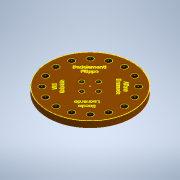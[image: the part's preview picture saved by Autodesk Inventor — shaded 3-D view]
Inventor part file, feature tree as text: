
AUTODESK INVENTOR PART (.ipt)
format: ipt  version: 2020.2 (Build 242310000, 310)  size: 1,744,896 bytes
history: native  units: mm
features: sketch x5, extrude x2, hole x2, other x1
ambient origin geometry x8: Origin, YZ Plane, XZ Plane, XY Plane, X Axis, Y Axis, Z Axis, Center Point
bodies: Solido1 (feature_tree)
feature tree (10):
  extrude  "Estrusione1"  Depth=80.0mm
  hole  "Foro1"  [1 undecoded]
  hole  "Foro2"  [1 undecoded]
  extrude  "Estrusione2"  TaperAngle=90.0deg  [1 undecoded]
  sketch  "Schizzo5"
  sketch  "Schizzo1"
  sketch  "Schizzo2"
  sketch  "Schizzo3"
  sketch  "Schizzo4"
  other  "Proietta spigoli di taglio1"
note: 3 required parameter values undecoded (feature->parameter linkage not recoverable at this tier; creation-order binding heuristic only, values carry confidence <= 0.55)
